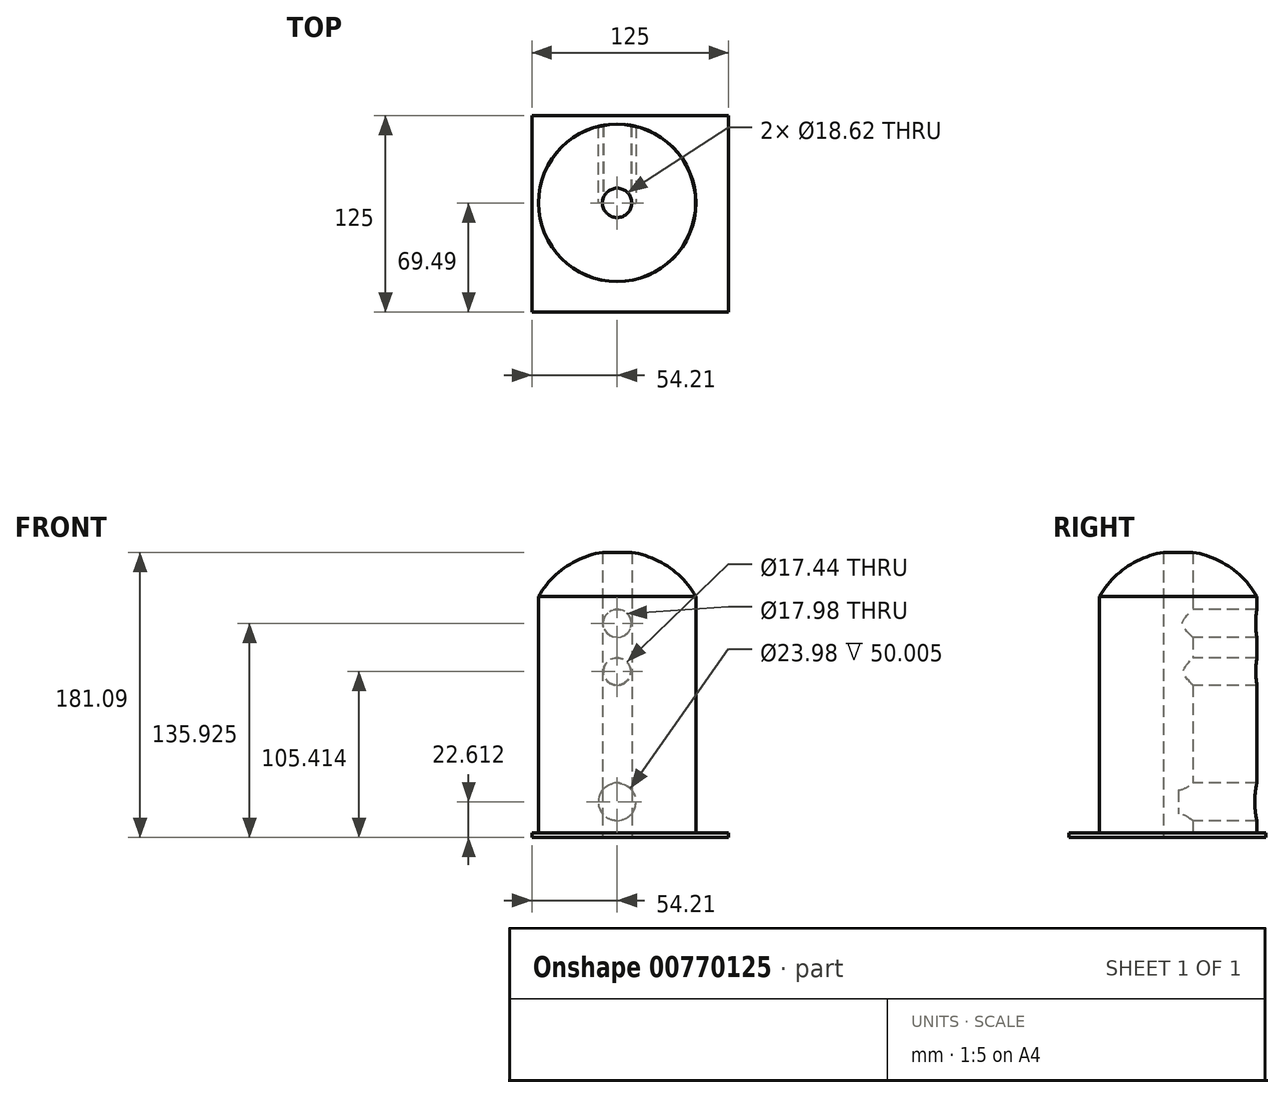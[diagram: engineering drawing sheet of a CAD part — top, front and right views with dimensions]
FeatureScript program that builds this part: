
annotation { "Feature Type Name" : "Feature", "Feature Type Description" : "" }
export const myFeature = defineFeature(function(context is Context, id is Id, definition is map)
    precondition{}
    {
        {
            var Q0;
            Q0=qCreatedBy(makeId("Top.planeOp"),FACE);
            var sketch = newSketch(context, id + "F0", { "sketchPlane" : qUnion([Q0])});
            skLineSegment(sketch, "E0.bottom", {"start": v(-54.21, 55.5) * mm, "end": v(70.79, 55.5) * mm});
            skLineSegment(sketch, "E0.top", {"start": v(-54.21, -69.5) * mm, "end": v(70.79, -69.5) * mm});
            skLineSegment(sketch, "E0.left", {"start": v(-54.21, 55.5) * mm, "end": v(-54.21, -69.5) * mm});
            skLineSegment(sketch, "E0.right", {"start": v(70.79, 55.5) * mm, "end": v(70.79, -69.5) * mm});
            skSolve(sketch);
        }
        {
            var Q0;
            Q0=makeQuery(id+"F0.imprint","IMPRINT",FACE,{"disambiguationData":[TD([[makeQuery(id+"F0.imprint","IMPRINT",EDGE,{"derivedFrom":sQuery(id+"F0.wireOp",EDGE,"E0.bottom")}),-1.0]])]});
            extrude(context, id + "F1", {"entities" : qUnion([Q0]), "depth" : 3 * mm, "offsetDistance" : 25.4 * mm});
        }
        {
            var Q0;
            Q0=makeQuery(id+"F1.opExtrude","CAP_FACE",FACE,{"disambiguationData":[OSD([sQuery(id+"F0.wireOp",EDGE,"E0.bottom"),sQuery(id+"F0.wireOp",EDGE,"E0.top"),sQuery(id+"F0.wireOp",EDGE,"E0.left"),sQuery(id+"F0.wireOp",EDGE,"E0.right")])],"isStart":false});
            var sketch = newSketch(context, id + "F2", { "sketchPlane" : qUnion([Q0])});
            skCircle(sketch, "E1", {"center": v(0, 0) * mm, "radius": 50 * mm});
            skSolve(sketch);
        }
        {
            var Q0;
            Q0=makeQuery(id+"F2.imprint","IMPRINT",FACE,{"disambiguationData":[TD([[makeQuery(id+"F2.imprint","IMPRINT",EDGE,{"derivedFrom":sQuery(id+"F2.wireOp",EDGE,"E1")}),1.0]])]});
            extrude(context, id + "F3", {"entities" : qUnion([Q0]), "operationType" : NewBodyOperationType.ADD, "depth" : 150 * mm, "offsetDistance" : 25.4 * mm});
        }
        {
            var Q0;
            Q0=qCreatedBy(makeId("Front.planeOp"),FACE);
            var sketch = newSketch(context, id + "F4", { "sketchPlane" : qUnion([Q0])});
            skLineSegment(sketch, "E2", {"start": v(-49.92, 153.14) * mm, "end": v(0, 153.14) * mm});
            skArc(sketch, "E3", {"start": v(0, 181.8) * mm, "mid": v(-28.82, 174.2) * mm, "end": v(-49.92, 153.14) * mm});
            skLineSegment(sketch, "E4", {"start": v(0, 181.8) * mm, "end": v(0, 89.04) * mm, "construction": true});
            skLineSegment(sketch, "E5", {"start": v(0, 153.14) * mm, "end": v(0, 181.8) * mm});
            skSolve(sketch);
        }
        {
            var Q0;
            Q0=makeQuery(id+"F4.imprint","IMPRINT",FACE,{"disambiguationData":[TD([[makeQuery(id+"F4.imprint","IMPRINT",EDGE,{"derivedFrom":sQuery(id+"F4.wireOp",EDGE,"E2")}),1.0]])]});
            var Q1;
            Q1=sQuery(id+"F4.wireOp",EDGE,"E4");
            var Q2;
            Q2=sQuery(id+"F4.wireOp",EDGE,"E3");
            var Q3;
            Q3=sQuery(id+"F4.wireOp",EDGE,"E2");
            var Q4;
            Q4=sQuery(id+"F4.wireOp",EDGE,"E4");
            revolve(context, id + "F5", {"operationType" : NewBodyOperationType.ADD, "surfaceOperationType" : NewSurfaceOperationType.NEW, "entities" : qUnion([Q0]), "surfaceEntities" : qUnion([Q1, Q2, Q3]), "axis" : qUnion([Q4]), "revolveType" : RevolveType.FULL});
        }
        {
            var Q0;
            Q0=qCreatedBy(makeId("Front.planeOp"),FACE);
            var sketch = newSketch(context, id + "F6", { "sketchPlane" : qUnion([Q0])});
            skCircle(sketch, "E6", {"center": v(0, 22.61) * mm, "radius": 12 * mm});
            skCircle(sketch, "E7", {"center": v(0, 135.93) * mm, "radius": 9 * mm});
            skCircle(sketch, "E8", {"center": v(0, 105.41) * mm, "radius": 8.72 * mm});
            skSolve(sketch);
        }
        {
            var Q0;
            Q0 = qSketchRegion(id + "F6", true);
            extrude(context, id + "F7", {"entities" : qUnion([Q0]), "operationType" : NewBodyOperationType.REMOVE, "oppositeDirection" : true, "depth" : 76.2 * mm, "offsetDistance" : 25.4 * mm});
        }
        {
            var Q0;
            Q0=qCreatedBy(makeId("Top.planeOp"),FACE);
            var sketch = newSketch(context, id + "F8", { "sketchPlane" : qUnion([Q0])});
            skCircle(sketch, "E9", {"center": v(0, 0) * mm, "radius": 9.3 * mm});
            skSolve(sketch);
        }
        {
            var Q0;
            Q0 = qSketchRegion(id + "F8", true);
            var Q1;
            Q1=makeQuery(id+"F5.opRevolve","SWEPT_FACE",FACE,{"disambiguationData":[OSD([sQuery(id+"F4.wireOp",EDGE,"E3")])]});
            extrude(context, id + "F9", {"entities" : qUnion([Q0]), "operationType" : NewBodyOperationType.REMOVE, "endBound" : BoundingType.THROUGH_ALL, "depth" : 152.4 * mm, "endBoundEntityFace" : qUnion([Q1]), "offsetDistance" : 25.4 * mm});
        }
    });
